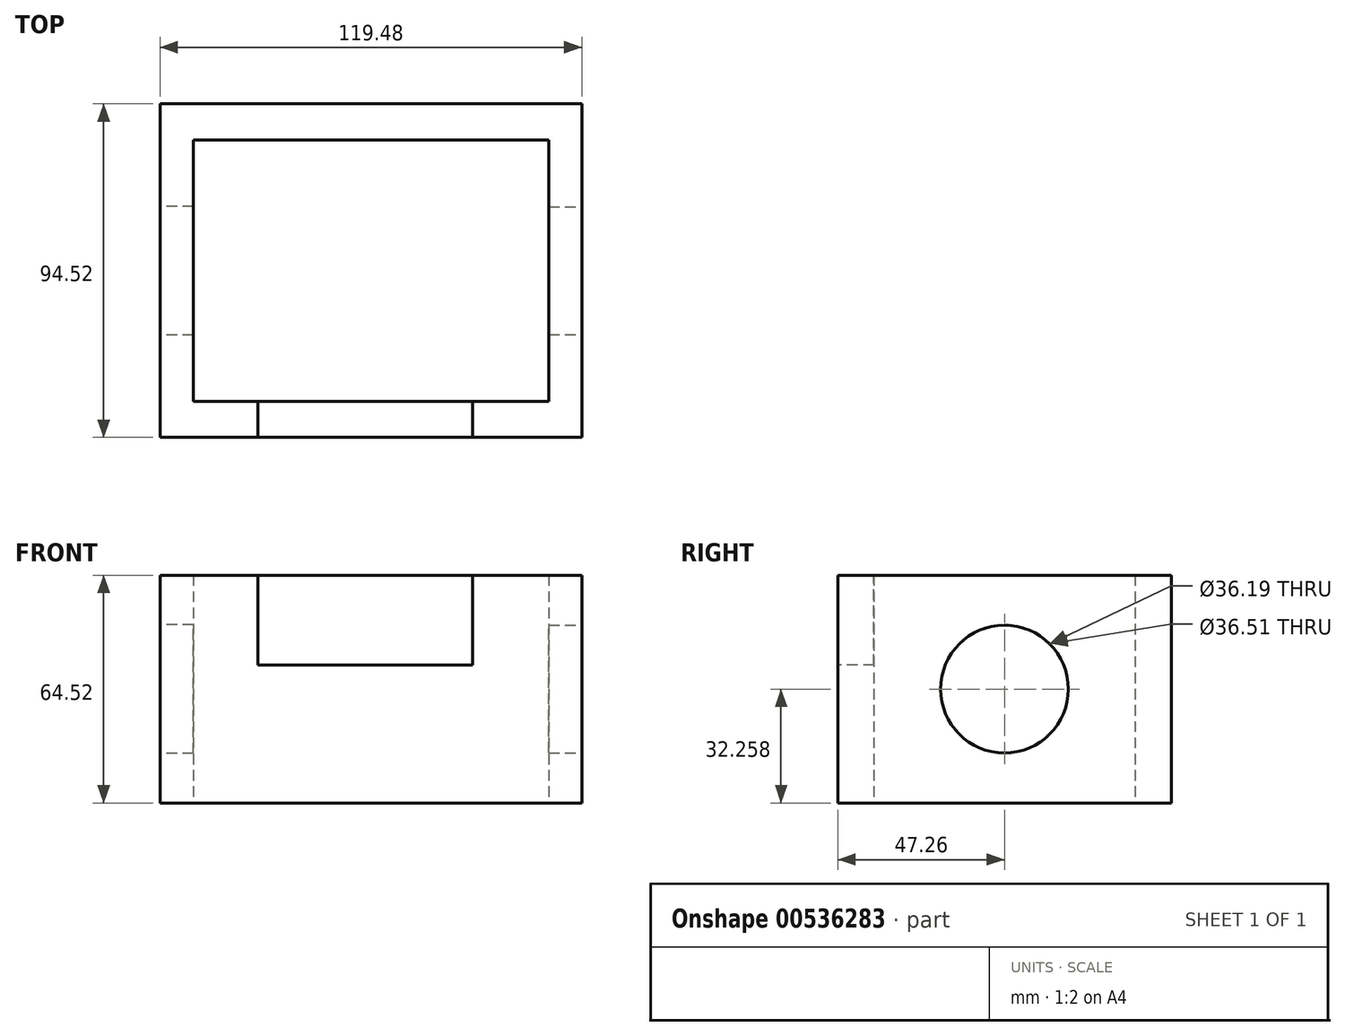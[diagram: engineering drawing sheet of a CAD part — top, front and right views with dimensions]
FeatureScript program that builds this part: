
annotation { "Feature Type Name" : "Feature", "Feature Type Description" : "" }
export const myFeature = defineFeature(function(context is Context, id is Id, definition is map)
    precondition{}
    {
        {
            var Q0;
            Q0=qCreatedBy(makeId("Top.planeOp"),FACE);
            var sketch = newSketch(context, id + "F0", { "sketchPlane" : qUnion([Q0])});
            skLineSegment(sketch, "E0.bottom", {"start": v(-59.74, 47.26) * mm, "end": v(59.74, 47.26) * mm});
            skLineSegment(sketch, "E0.top", {"start": v(-59.74, -47.26) * mm, "end": v(59.74, -47.26) * mm});
            skLineSegment(sketch, "E0.left", {"start": v(-59.74, 47.26) * mm, "end": v(-59.74, -47.26) * mm});
            skLineSegment(sketch, "E0.right", {"start": v(59.74, 47.26) * mm, "end": v(59.74, -47.26) * mm});
            skPoint(sketch, "E0.middle", {"position": v(0, 0) * mm});
            skLineSegment(sketch, "E1.bottom", {"start": v(-50.38, 37) * mm, "end": v(50.38, 37) * mm});
            skLineSegment(sketch, "E1.top", {"start": v(-50.38, -37) * mm, "end": v(50.38, -37) * mm});
            skLineSegment(sketch, "E1.left", {"start": v(-50.38, 37) * mm, "end": v(-50.38, -37) * mm});
            skLineSegment(sketch, "E1.right", {"start": v(50.38, 37) * mm, "end": v(50.38, -37) * mm});
            skSolve(sketch);
        }
        {
            var Q0;
            Q0=makeQuery(id+"F0.imprint","IMPRINT",FACE,{"disambiguationData":[TD([[makeQuery(id+"F0.imprint","IMPRINT",EDGE,{"derivedFrom":sQuery(id+"F0.wireOp",EDGE,"E0.bottom")}),-1.0]])]});
            extrude(context, id + "F1", {"entities" : qUnion([Q0]), "depth" : 64.52 * mm, "offsetDistance" : 25.4 * mm});
        }
        {
            var Q0;
            Q0=makeQuery(id+"F1.opExtrude","CAP_FACE",FACE,{"disambiguationData":[OSD([sQuery(id+"F0.wireOp",EDGE,"E0.bottom"),sQuery(id+"F0.wireOp",EDGE,"E0.top"),sQuery(id+"F0.wireOp",EDGE,"E0.left"),sQuery(id+"F0.wireOp",EDGE,"E0.right"),sQuery(id+"F0.wireOp",EDGE,"E1.bottom"),sQuery(id+"F0.wireOp",EDGE,"E1.top"),sQuery(id+"F0.wireOp",EDGE,"E1.left"),sQuery(id+"F0.wireOp",EDGE,"E1.right")])],"isStart":false});
            var sketch = newSketch(context, id + "F2", { "sketchPlane" : qUnion([Q0])});
            skLineSegment(sketch, "E2", {"start": v(28.82, -37) * mm, "end": v(28.82, -47.26) * mm});
            skLineSegment(sketch, "E3", {"start": v(-32.04, -47.26) * mm, "end": v(-32.04, -37) * mm});
            skPoint(sketch, "E4.0", {"position": v(-59.74, -47.26) * mm});
            skPoint(sketch, "E5.0", {"position": v(59.74, -47.26) * mm});
            skLineSegment(sketch, "E6.0", {"start": v(-59.74, -47.26) * mm, "end": v(59.74, -47.26) * mm});
            skSolve(sketch);
        }
        {
            var Q0;
            {var subQ0=sQuery(id+"F2.wireOp",EDGE,"E2");Q0=makeQuery(id+"F2.imprint","IMPRINT",FACE,{"disambiguationData":[TD([[makeQuery(id+"F2.imprint","IMPRINT",EDGE,{"derivedFrom":subQ0}),-1.0]])]});}
            extrude(context, id + "F3", {"entities" : qUnion([Q0]), "operationType" : NewBodyOperationType.REMOVE, "oppositeDirection" : true, "depth" : 25.4 * mm, "offsetDistance" : 25.4 * mm});
        }
        {
            var Q0;
            Q0=makeQuery(id+"F1.opExtrude","SWEPT_FACE",FACE,{"disambiguationData":[OSD([sQuery(id+"F0.wireOp",EDGE,"E0.right")])]});
            var sketch = newSketch(context, id + "F4", { "sketchPlane" : qUnion([Q0])});
            skCircle(sketch, "E7", {"center": v(0, 32.26) * mm, "radius": 18.1 * mm});
            skPoint(sketch, "E7.centerSnap0", {"position": v(-47.26, 32.26) * mm});
            skPoint(sketch, "E7.centerSnap1", {"position": v(0, 64.52) * mm});
            skSolve(sketch);
        }
        {
            var Q0;
            Q0=makeQuery(id+"F4.imprint","IMPRINT",FACE,{"disambiguationData":[TD([[makeQuery(id+"F4.imprint","IMPRINT",EDGE,{"derivedFrom":sQuery(id+"F4.wireOp",EDGE,"E7")}),1.0]])]});
            extrude(context, id + "F5", {"entities" : qUnion([Q0]), "operationType" : NewBodyOperationType.REMOVE, "oppositeDirection" : true, "depth" : 25.4 * mm, "offsetDistance" : 25.4 * mm});
        }
        {
            var Q0;
            Q0=makeQuery(id+"F1.opExtrude","SWEPT_FACE",FACE,{"disambiguationData":[OSD([sQuery(id+"F0.wireOp",EDGE,"E0.left")])]});
            var sketch = newSketch(context, id + "F6", { "sketchPlane" : qUnion([Q0])});
            skCircle(sketch, "E8", {"center": v(0, 32.26) * mm, "radius": 18.26 * mm});
            skPoint(sketch, "E8.centerSnap0", {"position": v(-47.26, 32.26) * mm});
            skPoint(sketch, "E8.centerSnap1", {"position": v(0, 64.52) * mm});
            skSolve(sketch);
        }
        {
            var Q0;
            Q0=makeQuery(id+"F6.imprint","IMPRINT",FACE,{"disambiguationData":[TD([[makeQuery(id+"F6.imprint","IMPRINT",EDGE,{"derivedFrom":sQuery(id+"F6.wireOp",EDGE,"E8")}),1.0]])]});
            extrude(context, id + "F7", {"entities" : qUnion([Q0]), "operationType" : NewBodyOperationType.REMOVE, "oppositeDirection" : true, "depth" : 25.4 * mm, "offsetDistance" : 25.4 * mm});
        }
    });
